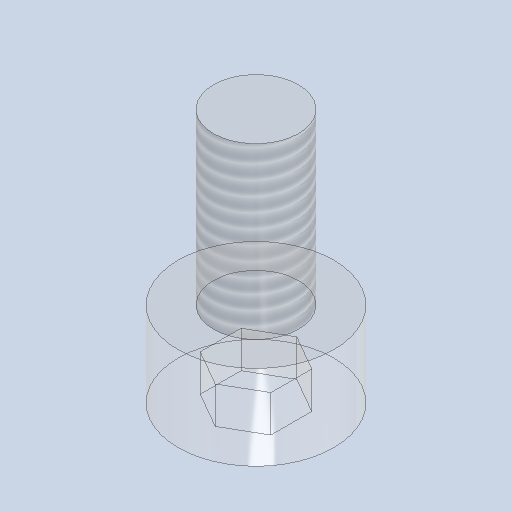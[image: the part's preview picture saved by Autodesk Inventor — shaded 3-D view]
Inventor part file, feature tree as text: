
AUTODESK INVENTOR PART (.ipt)
format: ipt  version: 2024.2 (Build 282272000, 272)  size: 155,136 bytes
history: native  units: mm
features: sketch x2, revolve x1, thread x1, extrude x1
ambient origin geometry x8: Origin, YZ Plane, XZ Plane, XY Plane, X Axis, Y Axis, Z Axis, Center Point
bodies: Solid1 (feature_tree)
feature tree (5):
  revolve  "Revolution1"  [1 undecoded]
  thread  "Thread1"  [1 undecoded]
  extrude  "Extrusion1"  [1 undecoded]
  sketch  "Sketch1"  dims[d4=90.0deg d5=6.0mm d6=0.0mm d0=0.0mm]
  sketch  "Sketch2"
note: 3 required parameter values undecoded (feature->parameter linkage not recoverable at this tier; creation-order binding heuristic only, values carry confidence <= 0.55)